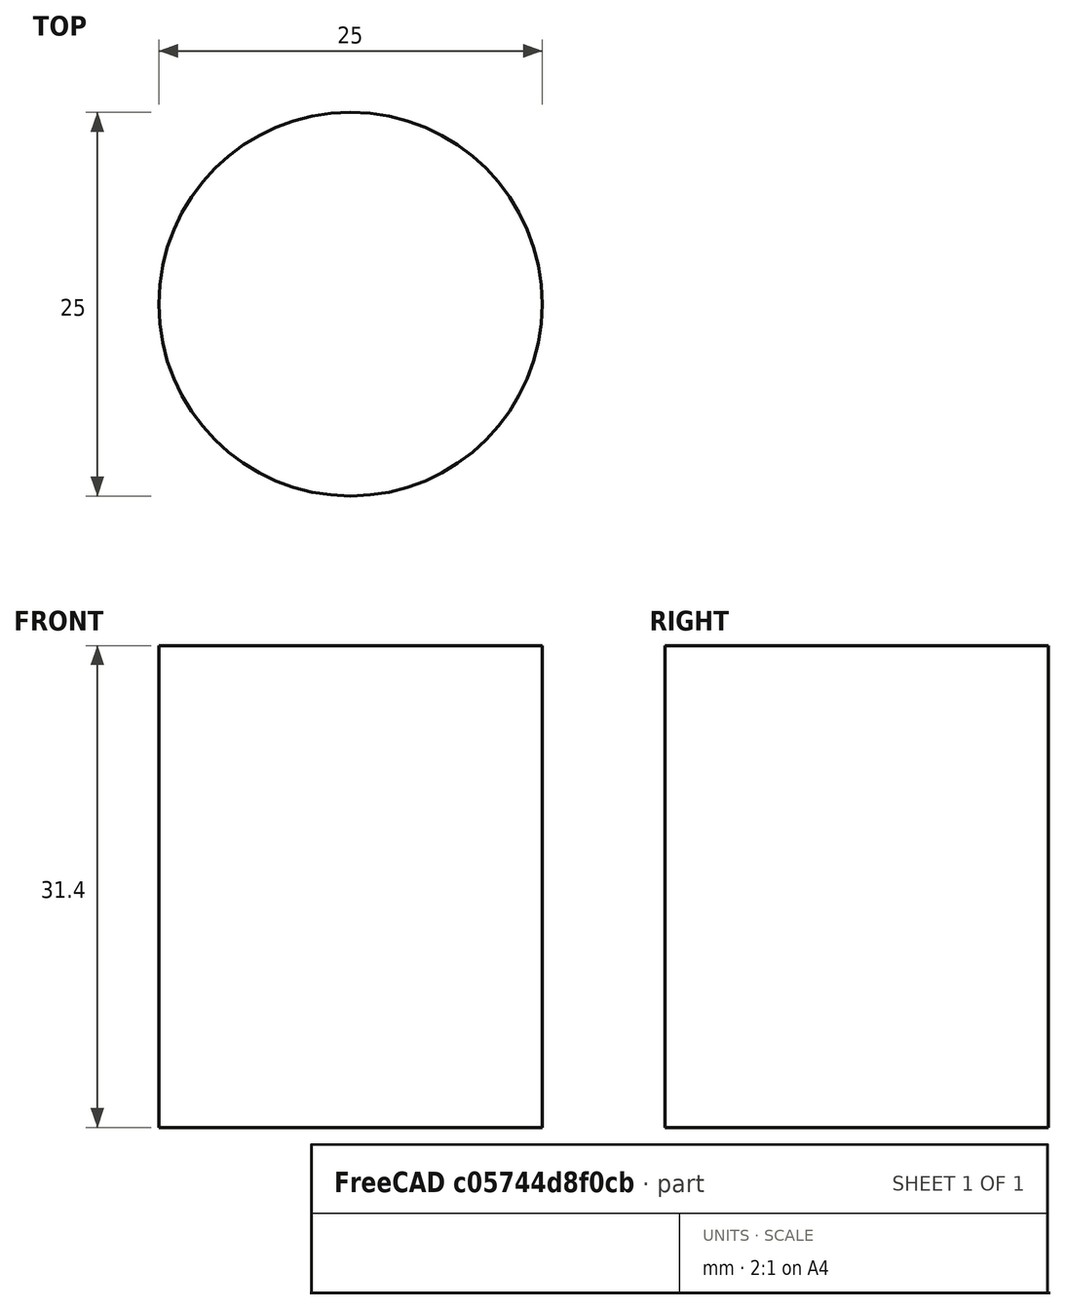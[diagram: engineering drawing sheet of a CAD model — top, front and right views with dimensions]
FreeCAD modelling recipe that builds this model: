
FCSTD DOCUMENT  (FreeCAD 0.18R15441 (Git))
Label: Hotend_E3D_Dummy_Outer
License: All rights reserved
LicenseURL: http://en.wikipedia.org/wiki/All_rights_reserved
objects: Sketcher::SketchObject×1, PartDesign::Pad×1, PartDesign::Body×1, App::Part×1
note: 4 computed .brp shape members not serialized (recipe doc carries the construction recipe); baked Part::Feature solids carry a one-line shape summary decoded from their .brp

FEATURE [Sketcher::SketchObject] Sketch002  label="DummyBaseSketch"
  MapMode = 5
  Support = -> [XY_Plane001]
  sketch-geometry (1):
    g0: Circle CenterX=0 CenterY=0 CenterZ=0 NormalX=0 NormalY=0 NormalZ=1 AngleXU=0 Radius=12.5
  constraints (2):
    c: Coincident(g0,g-1)
    c: Radius(g0) = 12.5
FEATURE [PartDesign::Pad] Pad002  label="DummyBasePad"
  Length = 30.4
  Length2 = 1
  Profile = -> Sketch002
  Type = 4
FEATURE [PartDesign::Body] Body  label="RadiatorBody"
  Group = -> [Sketch002,Pad002]
  Origin = -> Origin001
  Tip = -> Pad002
FEATURE [App::Part] Part  label="HotendPart"
  Group = -> [Body]
  License = CC BY 3.0
  LicenseURL = http://creativecommons.org/licenses/by/3.0/
  Origin = -> Origin
